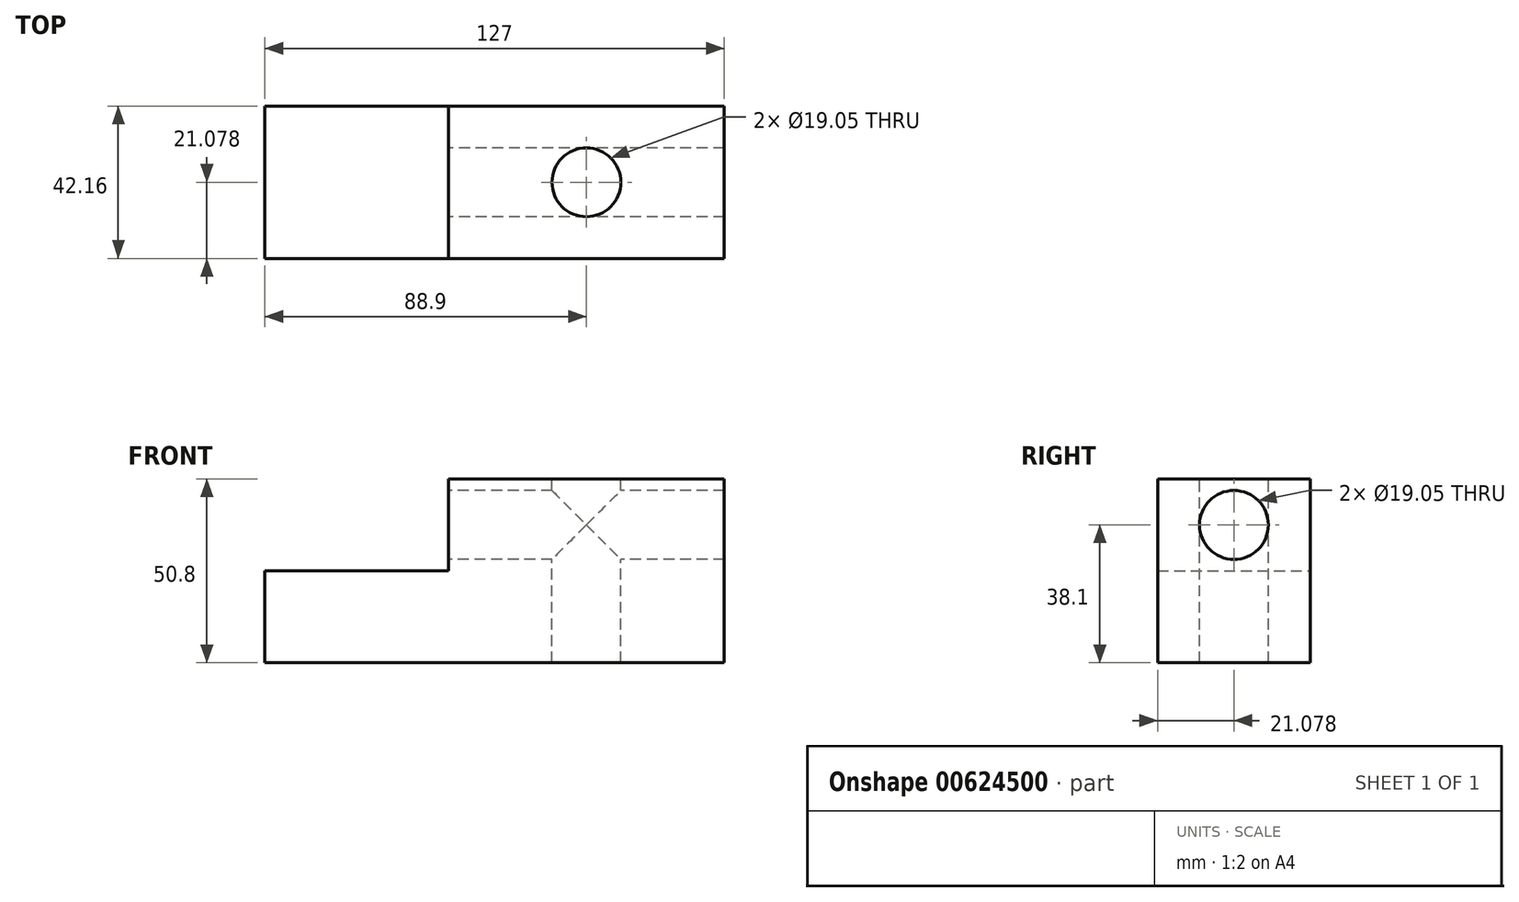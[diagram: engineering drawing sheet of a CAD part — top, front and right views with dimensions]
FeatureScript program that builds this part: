
annotation { "Feature Type Name" : "Feature", "Feature Type Description" : "" }
export const myFeature = defineFeature(function(context is Context, id is Id, definition is map)
    precondition{}
    {
        {
            var Q0;
            Q0=qCreatedBy(makeId("Front.planeOp"),FACE);
            var sketch = newSketch(context, id + "F0", { "sketchPlane" : qUnion([Q0])});
            skLineSegment(sketch, "E0.bottom", {"start": v(0, -80.2) * mm, "end": v(127, -80.2) * mm});
            skLineSegment(sketch, "E0.top", {"start": v(0, -131) * mm, "end": v(127, -131) * mm});
            skLineSegment(sketch, "E0.left", {"start": v(0, -80.2) * mm, "end": v(0, -131) * mm});
            skLineSegment(sketch, "E0.right", {"start": v(127, -80.2) * mm, "end": v(127, -131) * mm});
            skLineSegment(sketch, "E1", {"start": v(0, -105.6) * mm, "end": v(50.8, -105.6) * mm});
            skLineSegment(sketch, "E2", {"start": v(50.8, -105.6) * mm, "end": v(50.8, -80.2) * mm});
            skSolve(sketch);
        }
        {
            var Q0;
            {var subQ2=sQuery(id+"F0.wireOp",EDGE,"E0.top");Q0=makeQuery(id+"F0.imprint","IMPRINT",FACE,{"disambiguationData":[TD([[makeQuery(id+"F0.imprint","IMPRINT",EDGE,{"derivedFrom":subQ2}),1.0]])]});}
            extrude(context, id + "F1", {"entities" : qUnion([Q0]), "depth" : 42.16 * mm, "offsetDistance" : 25.4 * mm});
        }
        {
            var Q0;
            Q0=makeQuery(id+"F1.opExtrude","SWEPT_FACE",FACE,{"disambiguationData":[OSD([sQuery(id+"F0.wireOp",EDGE,"E2")])]});
            var sketch = newSketch(context, id + "F2", { "sketchPlane" : qUnion([Q0])});
            skPoint(sketch, "E3", {"position": v(21.08, -92.9) * mm});
            skPoint(sketch, "E3.positionSnap0", {"position": v(21.08, -80.2) * mm});
            skPoint(sketch, "E3.positionSnap1", {"position": v(42.16, -92.9) * mm});
            skSolve(sketch);
        }
        {
            var Q0;
            Q0=sQuery(id+"F2.wireOp",VERTEX,"E3");
            var Q1;
            Q1=makeQuery(id+"F1.opExtrude","SWEPT_BODY",BODY,{"disambiguationData":[OSD([sQuery(id+"F0.wireOp",EDGE,"E0.bottom"),sQuery(id+"F0.wireOp",EDGE,"E0.top"),sQuery(id+"F0.wireOp",EDGE,"E0.left"),sQuery(id+"F0.wireOp",EDGE,"E0.right"),sQuery(id+"F0.wireOp",EDGE,"E1"),sQuery(id+"F0.wireOp",EDGE,"E2")])]});
            hole(context, id + "F3", {"style" : HoleStyle.SIMPLE, "endStyle" : HoleEndStyle.THROUGH, "holeDiameter" : 19.05 * mm, "majorDiameter" : 6.35 * mm, "isTappedThrough" : true, "tappedDepth" : 12.7 * mm, "tapClearance" : 3, "locations" : qUnion([Q0]), "scope" : qUnion([Q1])});
        }
        {
            var Q0;
            Q0=makeQuery(id+"F1.opExtrude","SWEPT_FACE",FACE,{"disambiguationData":[OSD([sQuery(id+"F0.wireOp",EDGE,"E0.bottom")])]});
            var sketch = newSketch(context, id + "F4", { "sketchPlane" : qUnion([Q0])});
            skPoint(sketch, "E4", {"position": v(88.9, -21.08) * mm});
            skPoint(sketch, "E4.positionSnap0", {"position": v(88.9, -42.16) * mm});
            skPoint(sketch, "E4.positionSnap1", {"position": v(127, -21.08) * mm});
            skSolve(sketch);
        }
        {
            var Q0;
            Q0=sQuery(id+"F4.wireOp",VERTEX,"E4");
            var Q1;
            Q1=makeQuery(id+"F1.opExtrude","SWEPT_BODY",BODY,{"disambiguationData":[OSD([sQuery(id+"F0.wireOp",EDGE,"E0.bottom"),sQuery(id+"F0.wireOp",EDGE,"E0.top"),sQuery(id+"F0.wireOp",EDGE,"E0.left"),sQuery(id+"F0.wireOp",EDGE,"E0.right"),sQuery(id+"F0.wireOp",EDGE,"E1"),sQuery(id+"F0.wireOp",EDGE,"E2")])]});
            hole(context, id + "F5", {"style" : HoleStyle.SIMPLE, "endStyle" : HoleEndStyle.THROUGH, "holeDiameter" : 19.05 * mm, "majorDiameter" : 6.35 * mm, "isTappedThrough" : true, "tappedDepth" : 12.7 * mm, "tapClearance" : 3, "locations" : qUnion([Q0]), "scope" : qUnion([Q1])});
        }
    });
